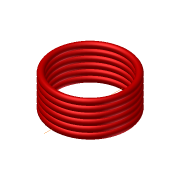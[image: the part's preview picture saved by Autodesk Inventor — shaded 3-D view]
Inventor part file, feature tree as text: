
AUTODESK INVENTOR PART (.ipt)
format: ipt  version: unknown  size: 317,440 bytes
history: native  units: in
note: dims shown in document units (in); Inventor stores cm internally (conversion verified against a paired STEP export)
features: revolve x1, pattern_linear x1, sketch x1
ambient origin geometry x8: Origin, YZ Plane, XZ Plane, XY Plane, X Axis, Y Axis, Z Axis, Center Point
feature tree (3):
  revolve  "Revolution3"  [1 undecoded]
  pattern_linear  "Rectangular Pattern1"  Spacing1=90.0deg  [1 undecoded]
  sketch  "Sketch23"  dims[d72=0.2362in d73=0.0394in d74=90.0deg d75=2.3622in d77=0.0394in]
note: 2 required parameter values undecoded (feature->parameter linkage not recoverable at this tier; creation-order binding heuristic only, values carry confidence <= 0.55)